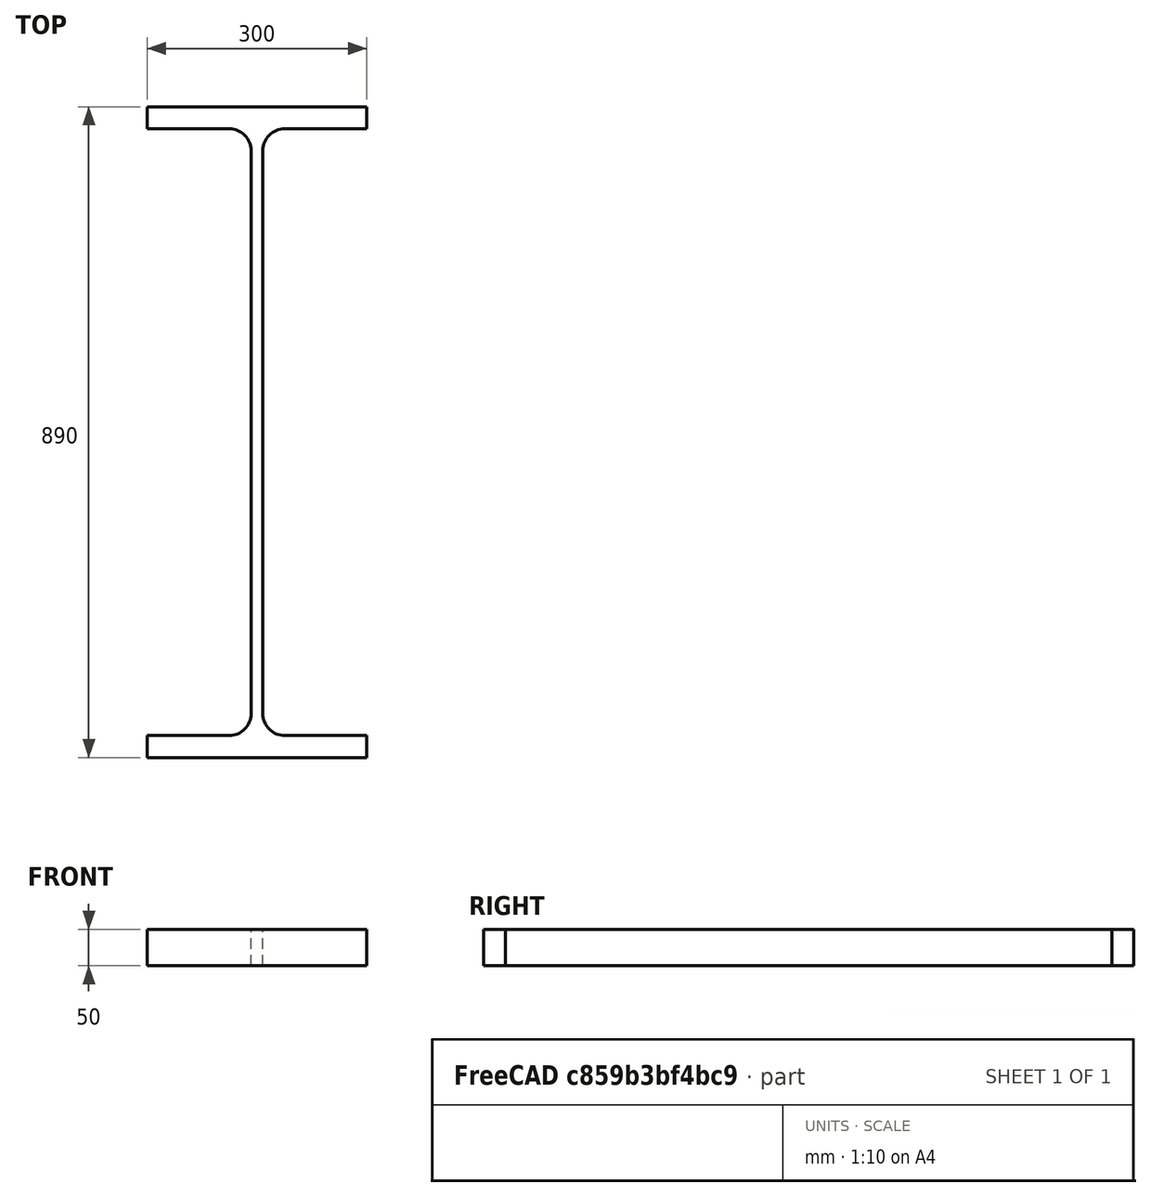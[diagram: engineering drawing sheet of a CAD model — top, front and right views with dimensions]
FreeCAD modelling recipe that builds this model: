
FCSTD DOCUMENT  (FreeCAD 0.15R4671 (Git))
Label: HE-A-Profile 900 DIN1025-3 S235JR
License: All rights reserved
LicenseURL: http://en.wikipedia.org/wiki/All_rights_reserved
objects: Sketcher::SketchObject×1, Part::Extrusion×1
note: 2 computed .brp shape members not serialized (recipe doc carries the construction recipe); baked Part::Feature solids carry a one-line shape summary decoded from their .brp

FEATURE [Sketcher::SketchObject] Sketch
  sketch-geometry (16):
    g0: LineSegment StartX=8 StartY=-385 StartZ=0 EndX=8 EndY=385 EndZ=0
    g1: LineSegment StartX=38 StartY=415 StartZ=0 EndX=150 EndY=415 EndZ=0
    g2: LineSegment StartX=150 StartY=415 StartZ=0 EndX=150 EndY=445 EndZ=0
    g3: LineSegment StartX=150 StartY=445 StartZ=0 EndX=-150 EndY=445 EndZ=0
    g4: LineSegment StartX=-150 StartY=445 StartZ=0 EndX=-150 EndY=415 EndZ=0
    g5: LineSegment StartX=-150 StartY=415 StartZ=0 EndX=-38 EndY=415 EndZ=0
    g6: LineSegment StartX=-8 StartY=385 StartZ=0 EndX=-8 EndY=-385 EndZ=0
    g7: LineSegment StartX=-38 StartY=-415 StartZ=0 EndX=-150 EndY=-415 EndZ=0
    g8: LineSegment StartX=-150 StartY=-415 StartZ=0 EndX=-150 EndY=-445 EndZ=0
    g9: LineSegment StartX=-150 StartY=-445 StartZ=0 EndX=150 EndY=-445 EndZ=0
    g10: LineSegment StartX=150 StartY=-445 StartZ=0 EndX=150 EndY=-415 EndZ=0
    g11: LineSegment StartX=150 StartY=-415 StartZ=0 EndX=38 EndY=-415 EndZ=0
    g12: ArcOfCircle CenterX=38 CenterY=385 CenterZ=0 NormalX=0 NormalY=0 NormalZ=1 Radius=30 StartAngle=1.5708 EndAngle=3.14159
    g13: ArcOfCircle CenterX=38 CenterY=-385 CenterZ=0 NormalX=0 NormalY=0 NormalZ=1 Radius=30 StartAngle=3.14159 EndAngle=4.71239
    g14: ArcOfCircle CenterX=-38 CenterY=385 CenterZ=0 NormalX=0 NormalY=0 NormalZ=1 Radius=30 StartAngle=0 EndAngle=1.5708
    g15: ArcOfCircle CenterX=-38 CenterY=-385 CenterZ=0 NormalX=0 NormalY=0 NormalZ=1 Radius=30 StartAngle=4.71239 EndAngle=6.28319
  constraints (42):
    c: Vertical(g0)
    c: Coincident(g2,g1)
    c: Vertical(g2)
    c: Coincident(g3,g2)
    c: Coincident(g4,g3)
    c: Vertical(g4)
    c: Coincident(g5,g4)
    c: Horizontal(g5)
    c: Vertical(g6)
    c: Horizontal(g7)
    c: Coincident(g8,g7)
    c: Vertical(g8)
    c: Coincident(g9,g8)
    c: Horizontal(g9)
    c: Coincident(g10,g9)
    c: Vertical(g10)
    c: Coincident(g11,g10)
    c: Horizontal(g11)
    c: Tangent(g1,g12) = 1.5708
    c: Tangent(g0,g12) = 1.5708
    c: Tangent(g0,g13) = 1.5708
    c: Tangent(g11,g13) = 1.5708
    c: Tangent(g5,g14) = 1.5708
    c: Tangent(g6,g14) = 1.5708
    c: Tangent(g6,g15) = 1.5708
    c: Tangent(g7,g15) = 1.5708
    c: Equal(g3,g9)
    c: Equal(g2,g4)
    c: Equal(g4,g8)
    c: Equal(g8,g10)
    c: Equal(g12,g14)
    c: Equal(g14,g15)
    c: Equal(g15,g13)
    c: Symmetric(g2,g3,g-2)
    c: Symmetric(g9,g8,g-2)
    c: Symmetric(g0,g6,g-2)
    c: Symmetric(g2,g9,g-1)
    c: DistanceY(g2,g9) = -890
    c: DistanceX(g3) = -300
    c: DistanceX(g0,g6) = -16
    c: DistanceY(g2) = 30
    c: Radius(g12) = 30
FEATURE [Part::Extrusion] Extrude  label="HE-A-Profile 900 DIN1025-3 S235JR"
  Base = -> Sketch
  Dir = (0,0,50)
  Solid = true
